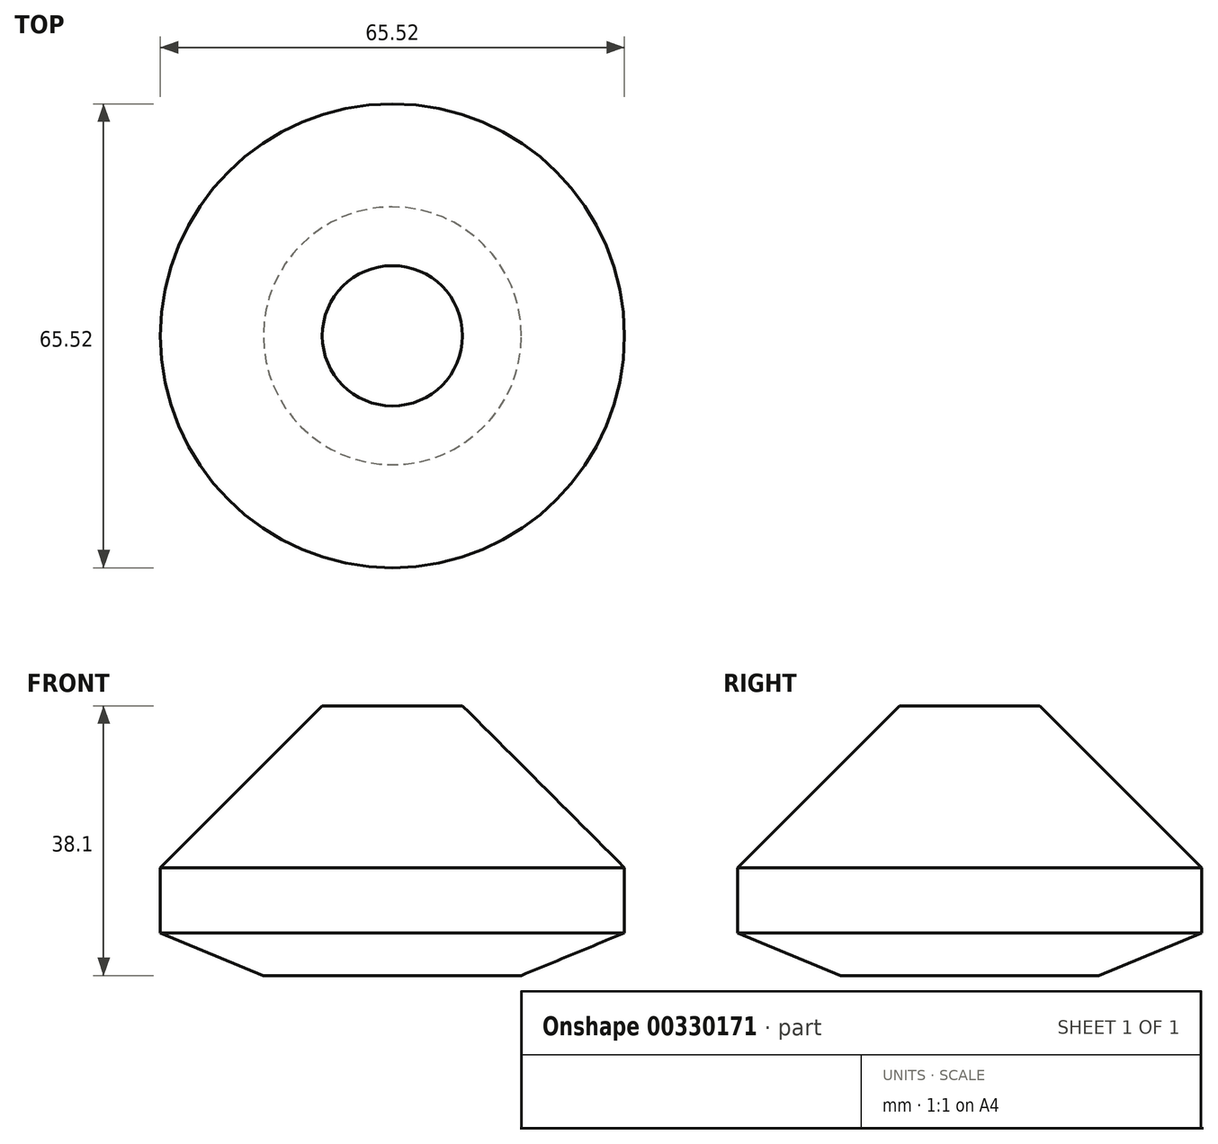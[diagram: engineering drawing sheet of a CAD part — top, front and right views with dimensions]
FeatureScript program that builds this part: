
annotation { "Feature Type Name" : "Feature", "Feature Type Description" : "" }
export const myFeature = defineFeature(function(context is Context, id is Id, definition is map)
    precondition{}
    {
        {
            var Q0;
            Q0=qCreatedBy(makeId("Top.planeOp"),FACE);
            var sketch = newSketch(context, id + "F0", { "sketchPlane" : qUnion([Q0])});
            skPoint(sketch, "E0", {"position": v(0, 0) * mm});
            skCircle(sketch, "E1", {"center": v(0, 0) * mm, "radius": 32.76 * mm});
            skSolve(sketch);
        }
        {
            var Q0;
            Q0=makeQuery(id+"F0.imprint","IMPRINT",FACE,{"disambiguationData":[TD([[makeQuery(id+"F0.imprint","IMPRINT",EDGE,{"derivedFrom":sQuery(id+"F0.wireOp",EDGE,"E1")}),1.0]])]});
            extrude(context, id + "F1", {"entities" : qUnion([Q0]), "depth" : 38.1 * mm});
        }
        {
            var Q0;
            Q0=makeQuery(id+"F1.opExtrude","CAP_EDGE",EDGE,{"disambiguationData":[OSD([sQuery(id+"F0.wireOp",EDGE,"E1")])],"isStart":false});
            chamfer(context, id + "F2", {"entities" : qUnion([Q0]), "width" : 22.86 * mm, "tangentPropagation" : true});
        }
        {
            var Q0;
            Q0=makeQuery(id+"F1.opExtrude","CAP_EDGE",EDGE,{"disambiguationData":[OSD([sQuery(id+"F0.wireOp",EDGE,"E1")])],"isStart":true});
            chamfer(context, id + "F3", {"entities" : qUnion([Q0]), "width" : 5.08 * mm, "tangentPropagation" : true});
        }
        {
            var Q0;
            {var subQ0=sQuery(id+"F0.wireOp",EDGE,"E1");Q0=makeQuery(id+"F3.opChamfer","BLEND_EDGE",EDGE,{"blendedFrom":[makeQuery(id+"F1.opExtrude","CAP_EDGE",EDGE,{"disambiguationData":[OSD([subQ0])],"isStart":true}),makeQuery(id+"F1.opExtrude","CAP_FACE",FACE,{"disambiguationData":[OSD([subQ0])],"isStart":true})],"blendedInto":[makeQuery(id+"F1.opExtrude","CAP_FACE",FACE,{"disambiguationData":[OSD([subQ0])],"isStart":true})]});}
            chamfer(context, id + "F4", {"entities" : qUnion([Q0]), "width" : 22.86 * mm, "tangentPropagation" : true});
        }
    });
